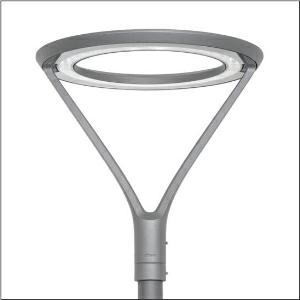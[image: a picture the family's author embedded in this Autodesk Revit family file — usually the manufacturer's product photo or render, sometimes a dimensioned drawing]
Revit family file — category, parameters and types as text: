
# Revit family: dl_r__20___pl1_2s_5xa51283ws008_843d
name_source: partatom
category: Lighting Fixtures
units: mm (PartAtom-declared; Revit-internal decimal feet)

## family parameters
Cut with Voids When Loaded = No
Host = Face
Light Source = No
Part Type = Normal
Room Calculation Point = No
Round Connector Dimension = Use Diameter
Shared = No

## types (1)
- --- (1 x LED, 3080 lm, 24.6 W, 3000K)
    Apparent Load = 25 VA
    CIE Flux Codes = 33 78 99 100 100
    Color Rendering = 70
    Color Temperature = 3000K
    Default Elevation = 1800 mm
    Description = DL® 20, mast luminaire, primary light control with reflector, highly specular, primary optical cover: cover, of toughened safety glass of clear glass with excellent transmission level, light distribution: PL1.2s, light emission: direct distribution, primary light characteristic: symmetric, installation type: post-top, LED, High Power LED, rated luminous flux: 3.040lm, luminous efficacy: 86lm/W, light colour: 730, colour temperature: 3000K, control gear: ECG Plus, control: overheat protection, power reduction, digital communication interface, constant luminous flux control, time-dependent luminous flux control, flexible luminous flux parameterisation, electronic power reduction, mains connection: 230..240V, 50/60Hz, connection cable pre-assembled, cable length: 5m, start of lifetime: 36W, end of service life: 36W, reduction: 17W, luminaire housing, upper part, of cast aluminium, powder-coated, Siteco® metallic grey (DB 702S), diameter: 690mm, height: 690mm, spigot size: 76mm (post-top), luminaire housing, of cast aluminium, powder-coated, Siteco® metallic grey (DB 702S), equipment: standard, protection rating (complete): IP66, insulation class (complete): insulation class II (safety insulation), certification: CE, ENEC, VDE, impact resistance: IK08, permissible operating ambient temperature: -25..+35°C, standard-compliant lighting for roads and squares, packaging unit: 1 piece

Light Distribution: PL1.2s
    Height = 690 mm
    Lamp = 1 x LED
    Lamp Light Flux = 3080 lm
    Lamp Power = 24.6 W
    Lamp count = 1
    Length = 690 mm
    Luminous efficacy = 125 lm/W
    Manufacturer = Siteco
    ModVariant = No
    Model = 5XA51283WS008
    Number of Poles = 1
    OnlyDefault = Yes
    Power Factor = 1
    Product Name = DL® 20 | PL1.2s
    Product group = mast luminaire | pylon top
    ProductGroupID = 6100
    Protection Class = Protection class II
    Protection Degree = IP 66
    RLX_Detail_Level = 1
    RLX_Emergency_Light_Flux = 0 lm
    RLX_Emergency_Type = 0
    RLX_Emergency_Type_DB = No
    RlxData = <blob elided: 204941 chars, md5=b2b52be5>
    Socket = socket
    Standby Power = 0 W
    System Light Flux = 3080 lm
    System Power = 25 W
    Type Comments = factory setting: luminous flux: 100 % | dim-lin: 254 | 330 mA
    Type Image = l_1006001.jpg
    URL = http://relux.com
    VarID = @adj_045955
    Voltage = 0 V
    Weight = 0.00 kg
    Width = 0 mm  [stored 0 ft]

note: [stored X ft] marks values corroborated as IEEE doubles in the binary element streams (Revit-internal decimal feet)

## geometry (parser evidence)
native form markers: Blend x4, Sweep x10
no freeform markers — native parametric forms only
